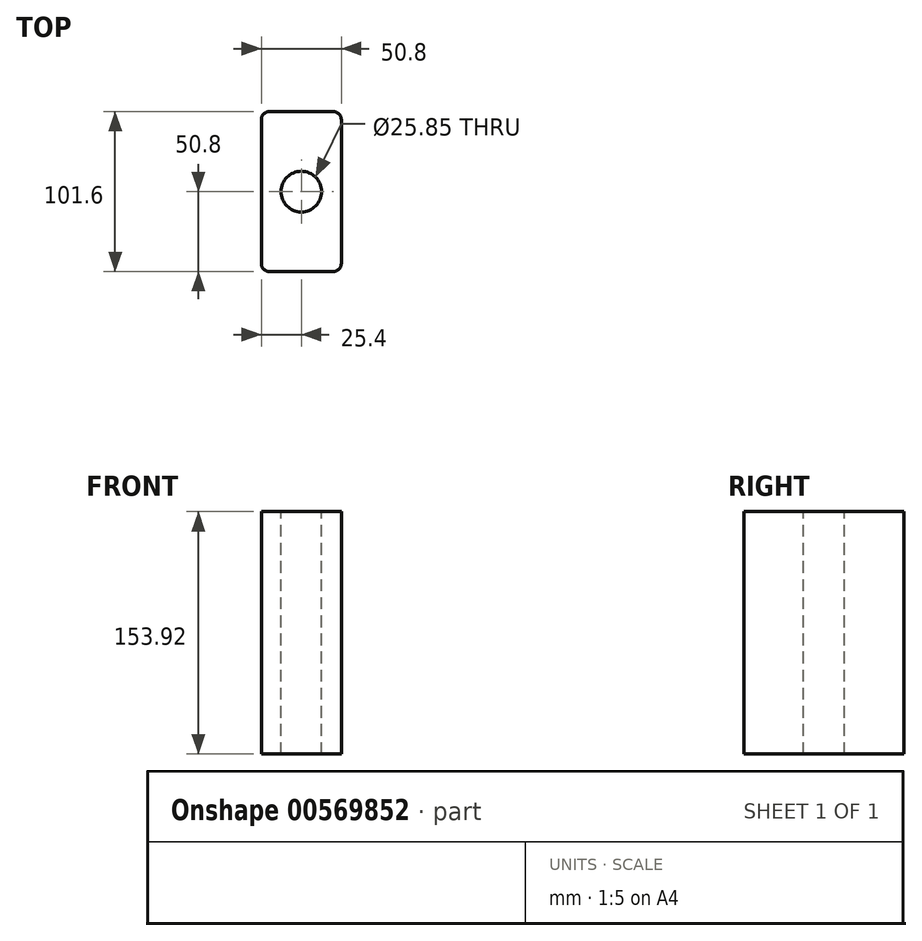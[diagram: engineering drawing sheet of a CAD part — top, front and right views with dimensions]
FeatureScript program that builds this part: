
annotation { "Feature Type Name" : "Feature", "Feature Type Description" : "" }
export const myFeature = defineFeature(function(context is Context, id is Id, definition is map)
    precondition{}
    {
        {
            var Q0;
            Q0=qCreatedBy(makeId("Top.planeOp"),FACE);
            var sketch = newSketch(context, id + "F0", { "sketchPlane" : qUnion([Q0])});
            skLineSegment(sketch, "E0.bottom", {"start": v(0, 0) * mm, "end": v(50.8, 0) * mm});
            skLineSegment(sketch, "E0.top", {"start": v(0, 101.6) * mm, "end": v(50.8, 101.6) * mm});
            skLineSegment(sketch, "E0.left", {"start": v(0, 0) * mm, "end": v(0, 101.6) * mm});
            skLineSegment(sketch, "E0.right", {"start": v(50.8, 0) * mm, "end": v(50.8, 101.6) * mm});
            skCircle(sketch, "E1", {"center": v(25.4, 50.8) * mm, "radius": 12.92 * mm});
            skLineSegment(sketch, "E2", {"start": v(0, 50.8) * mm, "end": v(50.8, 50.8) * mm, "construction": true});
            skLineSegment(sketch, "E3", {"start": v(25.4, 101.6) * mm, "end": v(25.4, 0) * mm, "construction": true});
            skSolve(sketch);
        }
        {
            var Q0;
            Q0=makeQuery(id+"F0.imprint","IMPRINT",FACE,{"disambiguationData":[TD([[makeQuery(id+"F0.imprint","IMPRINT",EDGE,{"derivedFrom":sQuery(id+"F0.wireOp",EDGE,"E0.bottom")}),1.0]])]});
            extrude(context, id + "F1", {"entities" : qUnion([Q0]), "oppositeDirection" : true, "depth" : 153.92 * mm, "offsetDistance" : 25.4 * mm});
        }
        {
            var Q0;
            Q0=makeQuery(id+"F1.opExtrude","SWEPT_EDGE",EDGE,{"disambiguationData":[OSD([sQuery(id+"F0.wireOp",EDGE,"E0.bottom"),sQuery(id+"F0.wireOp",EDGE,"E0.right")])]});
            var Q1;
            Q1=makeQuery(id+"F1.opExtrude","SWEPT_EDGE",EDGE,{"disambiguationData":[OSD([sQuery(id+"F0.wireOp",EDGE,"E0.top"),sQuery(id+"F0.wireOp",EDGE,"E0.right")])]});
            var Q2;
            Q2=makeQuery(id+"F1.opExtrude","SWEPT_EDGE",EDGE,{"disambiguationData":[OSD([sQuery(id+"F0.wireOp",EDGE,"E0.bottom"),sQuery(id+"F0.wireOp",EDGE,"E0.left")])]});
            var Q3;
            Q3=makeQuery(id+"F1.opExtrude","SWEPT_EDGE",EDGE,{"disambiguationData":[OSD([sQuery(id+"F0.wireOp",EDGE,"E0.top"),sQuery(id+"F0.wireOp",EDGE,"E0.left")])]});
            fillet(context, id + "F2", {"entities" : qUnion([Q0, Q1, Q2, Q3]), "radius" : 5.08 * mm, "tangentPropagation" : true, "allowEdgeOverflow" : false});
        }
    });
